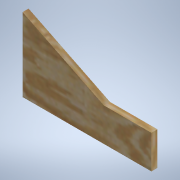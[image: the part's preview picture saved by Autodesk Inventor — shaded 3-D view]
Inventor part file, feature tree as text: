
AUTODESK INVENTOR PART (.ipt)
format: ipt  version: 2021.1 (Build 251245000, 245)  size: 115,200 bytes
history: native  units: mm
features: other x3, extrude x1, sketch x1, reference x1
ambient origin geometry x8: Origin, YZ Plane, XZ Plane, XY Plane, X Axis, Y Axis, Z Axis, Center Point
bodies: Solid1 (feature_tree)
feature tree (6):
  extrude  "Extrusion1"  [1 undecoded]
  sketch  "Sketch1"  dims[d1=12.7mm d2=0.0mm]
  reference  "Reference1"
  other  "<userpath>\Documents\Kerbal Kontroller\Design\Final\Inventor\Final.iam"
  other  "Final.iam"
  other  "Bottom:1"
note: 1 required parameter value undecoded (feature->parameter linkage not recoverable at this tier; creation-order binding heuristic only, values carry confidence <= 0.55)
